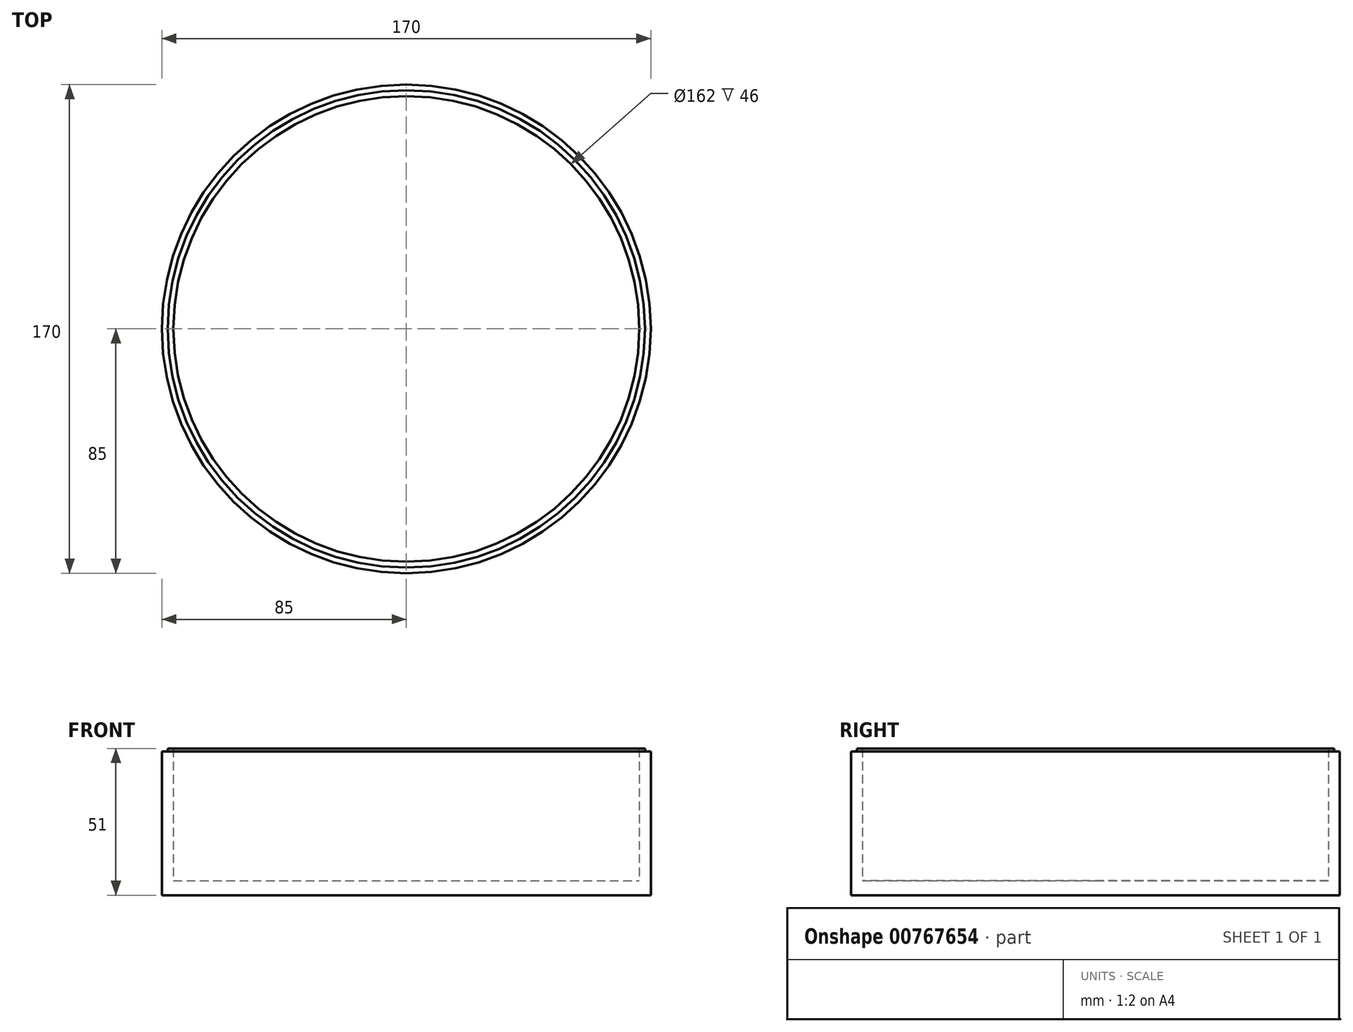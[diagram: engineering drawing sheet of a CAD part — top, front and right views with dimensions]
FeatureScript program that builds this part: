
annotation { "Feature Type Name" : "Feature", "Feature Type Description" : "" }
export const myFeature = defineFeature(function(context is Context, id is Id, definition is map)
    precondition{}
    {
        {
            var Q0;
            Q0=qCreatedBy(makeId("Front.planeOp"),FACE);
            var sketch = newSketch(context, id + "F0", { "sketchPlane" : qUnion([Q0])});
            skLineSegment(sketch, "E0", {"start": v(-83, 16.08) * mm, "end": v(-85, 16.08) * mm});
            skLineSegment(sketch, "E1", {"start": v(-85, 16.08) * mm, "end": v(-85, -33.92) * mm});
            skLineSegment(sketch, "E2", {"start": v(-85, -33.92) * mm, "end": v(0, -33.92) * mm});
            skLineSegment(sketch, "E3", {"start": v(0, -33.92) * mm, "end": v(0, -28.92) * mm});
            skLineSegment(sketch, "E4", {"start": v(0, -28.92) * mm, "end": v(-81, -28.92) * mm});
            skLineSegment(sketch, "E5", {"start": v(-81, -28.92) * mm, "end": v(-81, 17.08) * mm});
            skLineSegment(sketch, "E6", {"start": v(-83, 16.08) * mm, "end": v(-83, 17.08) * mm});
            skLineSegment(sketch, "E7", {"start": v(-83, 17.08) * mm, "end": v(-81, 17.08) * mm});
            skSolve(sketch);
        }
        {
            var Q0;
            Q0=makeQuery(id+"F0.imprint","IMPRINT",FACE,{"disambiguationData":[TD([[makeQuery(id+"F0.imprint","IMPRINT",EDGE,{"derivedFrom":sQuery(id+"F0.wireOp",EDGE,"E0")}),1.0]])]});
            var Q1;
            Q1=sQuery(id+"F0.wireOp",EDGE,"E3");
            revolve(context, id + "F1", {"surfaceOperationType" : NewSurfaceOperationType.NEW, "entities" : qUnion([Q0]), "axis" : qUnion([Q1]), "revolveType" : RevolveType.FULL});
        }
    });
